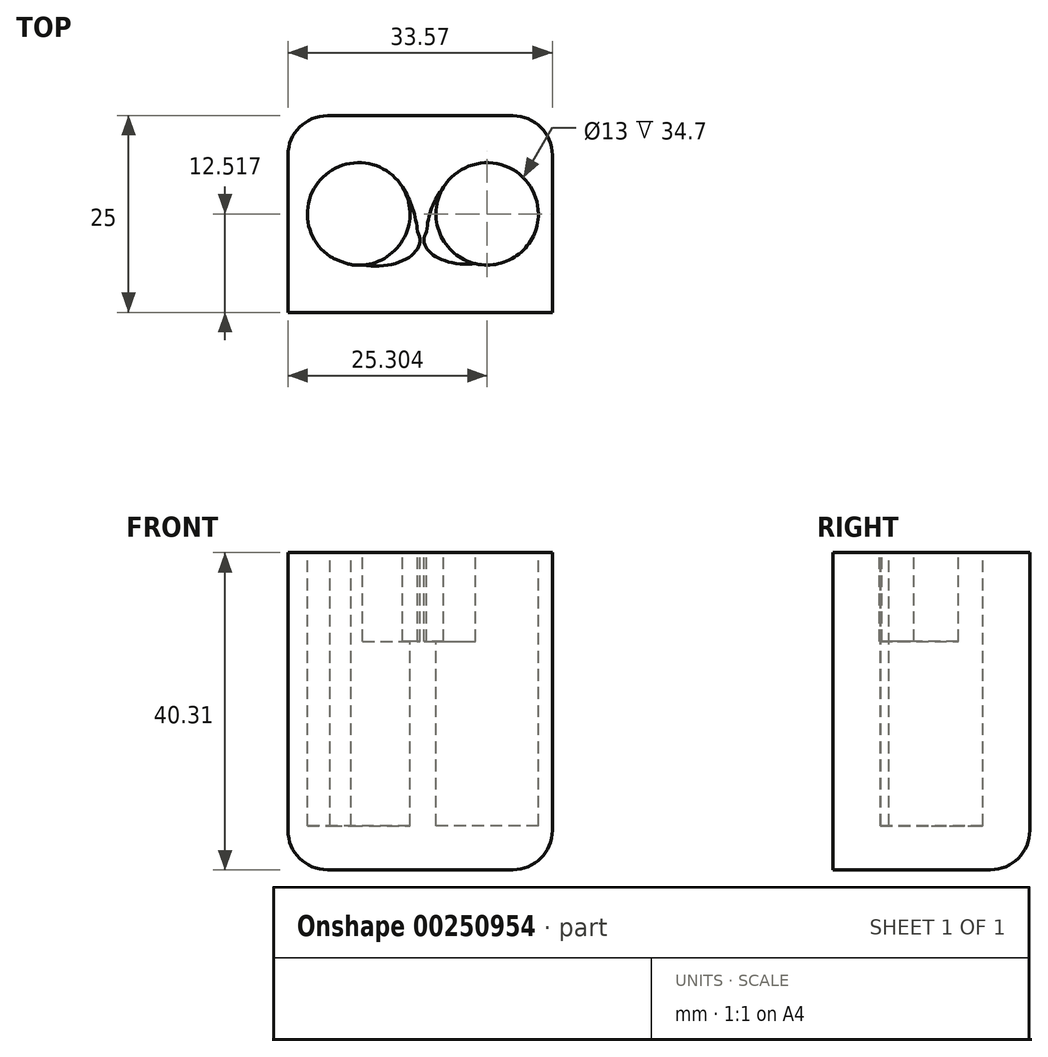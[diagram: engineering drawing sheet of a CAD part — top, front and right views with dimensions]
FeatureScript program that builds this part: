
annotation { "Feature Type Name" : "Feature", "Feature Type Description" : "" }
export const myFeature = defineFeature(function(context is Context, id is Id, definition is map)
    precondition{}
    {
        {
            var Q0;
            Q0=qCreatedBy(makeId("Front.planeOp"),FACE);
            var sketch = newSketch(context, id + "F0", { "sketchPlane" : qUnion([Q0])});
            skLineSegment(sketch, "E0.bottom", {"start": v(0, 0) * mm, "end": v(-33.57, 0) * mm});
            skLineSegment(sketch, "E0.top", {"start": v(0, -40.3) * mm, "end": v(-33.57, -40.3) * mm});
            skLineSegment(sketch, "E0.left", {"start": v(0, 0) * mm, "end": v(0, -40.3) * mm});
            skLineSegment(sketch, "E0.right", {"start": v(-33.57, 0) * mm, "end": v(-33.57, -40.3) * mm});
            skSolve(sketch);
        }
        {
            var Q0;
            Q0=makeQuery(id+"F0.imprint","IMPRINT",FACE,{"disambiguationData":[TD([[makeQuery(id+"F0.imprint","IMPRINT",EDGE,{"derivedFrom":sQuery(id+"F0.wireOp",EDGE,"E0.bottom")}),1.0]])]});
            extrude(context, id + "F1", {"entities" : qUnion([Q0]), "depth" : 25 * mm});
        }
        {
            var Q0;
            Q0=makeQuery(id+"F1.opExtrude","CAP_EDGE",EDGE,{"disambiguationData":[OSD([sQuery(id+"F0.wireOp",EDGE,"E0.left")])],"isStart":true});
            var Q1;
            Q1=makeQuery(id+"F1.opExtrude","CAP_EDGE",EDGE,{"disambiguationData":[OSD([sQuery(id+"F0.wireOp",EDGE,"E0.right")])],"isStart":true});
            var Q2;
            Q2=makeQuery(id+"F1.opExtrude","CAP_EDGE",EDGE,{"disambiguationData":[OSD([sQuery(id+"F0.wireOp",EDGE,"E0.top")])],"isStart":true});
            var Q3;
            Q3=makeQuery(id+"F1.opExtrude","SWEPT_EDGE",EDGE,{"disambiguationData":[OSD([sQuery(id+"F0.wireOp",EDGE,"E0.top"),sQuery(id+"F0.wireOp",EDGE,"E0.right")])]});
            var Q4;
            Q4=makeQuery(id+"F1.opExtrude","SWEPT_EDGE",EDGE,{"disambiguationData":[OSD([sQuery(id+"F0.wireOp",EDGE,"E0.top"),sQuery(id+"F0.wireOp",EDGE,"E0.left")])]});
            fillet(context, id + "F2", {"entities" : qUnion([Q0, Q1, Q2, Q3, Q4]), "radius" : 5 * mm, "tangentPropagation" : true, "allowEdgeOverflow" : false});
        }
        {
            var Q0;
            Q0=makeQuery(id+"F1.opExtrude","SWEPT_FACE",FACE,{"disambiguationData":[OSD([sQuery(id+"F0.wireOp",EDGE,"E0.bottom")])]});
            var sketch = newSketch(context, id + "F3", { "sketchPlane" : qUnion([Q0])});
            skCircle(sketch, "E1", {"center": v(-24.6, -12.48) * mm, "radius": 6.52 * mm});
            skCircle(sketch, "E2", {"center": v(-8.27, -12.48) * mm, "radius": 6.5 * mm});
            skEllipse(sketch, "E3", {"center": v(-22.46, -15.82) * mm, "majorRadius": 5.64 * mm, "minorRadius": 3.3 * mm, "majorAxis": v(1, 0)});
            skArc(sketch, "E4", {"start": v(-28.23, -17.89) * mm, "mid": v(-25.11, -19.02) * mm, "end": v(-21.8, -19.1) * mm});
            skEllipse(sketch, "E5", {"center": v(-10.8, -15.82) * mm, "majorRadius": 5.5 * mm, "minorRadius": 3.06 * mm, "majorAxis": v(-1, 0)});
            skPoint(sketch, "E5.centerSnap0", {"position": v(-16.82, -15.82) * mm});
            skArc(sketch, "E6", {"start": v(-12.62, -18.7) * mm, "mid": v(-9.42, -19.25) * mm, "end": v(-6.22, -18.65) * mm});
            skArc(sketch, "E7", {"start": v(-17.12, -14.75) * mm, "mid": v(-17.74, -11.8) * mm, "end": v(-19.04, -9.07) * mm});
            skArc(sketch, "E8", {"start": v(-13.8, -9.07) * mm, "mid": v(-15.3, -11.74) * mm, "end": v(-15.95, -14.75) * mm});
            skSolve(sketch);
        }
        {
            var Q0;
            {var subQ0=sQuery(id+"F3.wireOp",EDGE,"E5");var subQ1=sQuery(id+"F3.wireOp",EDGE,"E2");var subQ2=makeQuery(id+"F3.imprint","INTERSECT",VERTEX,{"disambiguationData":[OD(0.0)],"derivedFrom":[subQ1,subQ0]});Q0=makeQuery(id+"F3.imprint","IMPRINT",FACE,{"disambiguationData":[TD([[makeQuery(id+"F3.imprint","IMPRINT",EDGE,{"disambiguationData":[TD([[subQ2,-1.0]])],"derivedFrom":subQ1}),1.0]])]});}
            var Q1;
            {var subQ0=sQuery(id+"F3.wireOp",EDGE,"E2");var subQ1=makeQuery(id+"F3.imprint","INTERSECT",VERTEX,{"derivedFrom":[subQ0,sQuery(id+"F3.wireOp",EDGE,"E8")]});Q1=makeQuery(id+"F3.imprint","IMPRINT",FACE,{"disambiguationData":[TD([[makeQuery(id+"F3.imprint","IMPRINT",EDGE,{"disambiguationData":[TD([[subQ1,-1.0]])],"derivedFrom":subQ0}),1.0]])]});}
            var Q2;
            {var subQ0=sQuery(id+"F3.wireOp",EDGE,"E3");var subQ1=sQuery(id+"F3.wireOp",EDGE,"E1");var subQ2=makeQuery(id+"F3.imprint","INTERSECT",VERTEX,{"disambiguationData":[OD(0.0)],"derivedFrom":[subQ1,subQ0]});Q2=makeQuery(id+"F3.imprint","IMPRINT",FACE,{"disambiguationData":[TD([[makeQuery(id+"F3.imprint","IMPRINT",EDGE,{"disambiguationData":[TD([[subQ2,-1.0]])],"derivedFrom":subQ1}),1.0]])]});}
            var Q3;
            {var subQ0=sQuery(id+"F3.wireOp",EDGE,"E1");var subQ4=sQuery(id+"F3.wireOp",EDGE,"E4");var subQ7=makeQuery(id+"F3.imprint","INTERSECT",VERTEX,{"disambiguationData":[OD(0.0)],"derivedFrom":[subQ0,subQ4]});Q3=makeQuery(id+"F3.imprint","IMPRINT",FACE,{"disambiguationData":[TD([[makeQuery(id+"F3.imprint","IMPRINT",EDGE,{"disambiguationData":[TD([[subQ7,1.0]])],"derivedFrom":subQ0}),1.0]])]});}
            extrude(context, id + "F4", {"entities" : qUnion([Q0, Q1, Q2, Q3]), "operationType" : NewBodyOperationType.REMOVE, "oppositeDirection" : true, "depth" : 34.7 * mm});
        }
        {
            var Q0;
            {var subQ0=sQuery(id+"F3.wireOp",EDGE,"E7");Q0=makeQuery(id+"F3.imprint","IMPRINT",FACE,{"disambiguationData":[TD([[makeQuery(id+"F3.imprint","IMPRINT",EDGE,{"derivedFrom":subQ0}),1.0]])]});}
            var Q1;
            {var subQ0=sQuery(id+"F3.wireOp",EDGE,"E3");var subQ1=sQuery(id+"F3.wireOp",EDGE,"E1");var subQ2=makeQuery(id+"F3.imprint","INTERSECT",VERTEX,{"disambiguationData":[OD(0.0)],"derivedFrom":[subQ1,subQ0]});Q1=makeQuery(id+"F3.imprint","IMPRINT",FACE,{"disambiguationData":[TD([[makeQuery(id+"F3.imprint","IMPRINT",EDGE,{"disambiguationData":[TD([[subQ2,-1.0]])],"derivedFrom":subQ1}),-1.0]])]});}
            var Q2;
            {var subQ0=sQuery(id+"F3.wireOp",EDGE,"E5");var subQ1=sQuery(id+"F3.wireOp",EDGE,"E2");var subQ2=makeQuery(id+"F3.imprint","INTERSECT",VERTEX,{"disambiguationData":[OD(0.0)],"derivedFrom":[subQ1,subQ0]});Q2=makeQuery(id+"F3.imprint","IMPRINT",FACE,{"disambiguationData":[TD([[makeQuery(id+"F3.imprint","IMPRINT",EDGE,{"disambiguationData":[TD([[subQ2,-1.0]])],"derivedFrom":subQ1}),-1.0]])]});}
            var Q3;
            {var subQ0=sQuery(id+"F3.wireOp",EDGE,"E8");Q3=makeQuery(id+"F3.imprint","IMPRINT",FACE,{"disambiguationData":[TD([[makeQuery(id+"F3.imprint","IMPRINT",EDGE,{"derivedFrom":subQ0}),1.0]])]});}
            extrude(context, id + "F5", {"entities" : qUnion([Q0, Q1, Q2, Q3]), "operationType" : NewBodyOperationType.REMOVE, "oppositeDirection" : true, "depth" : 11.3 * mm});
        }
    });
